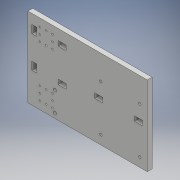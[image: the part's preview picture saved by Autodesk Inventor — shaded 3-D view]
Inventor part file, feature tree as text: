
AUTODESK INVENTOR PART (.ipt)
format: ipt  version: 2017 (Build 210142000, 142)  size: 223,232 bytes
history: native  units: mm
features: sketch x4, extrude x4, other x1, projected_geometry x1
ambient origin geometry x8: Origin, YZ Plane, XZ Plane, XY Plane, X Axis, Y Axis, Z Axis, Center Point
bodies: Body1 (feature_tree)
feature tree (10):
  sketch  "Esquisse1"
  other  "Plan de construction1"
  extrude  "Extrusion2"  Depth=150.0mm
  extrude  "Extrusion3"  Depth=100.0mm
  extrude  "Extrusion4"  Depth=2.1mm
  extrude  "Extrusion5"  Depth=10.0mm
  sketch  "Esquisse3"
  projected_geometry  "Boucle projetée2"
  sketch  "Esquisse4"
  sketch  "Esquisse5"
